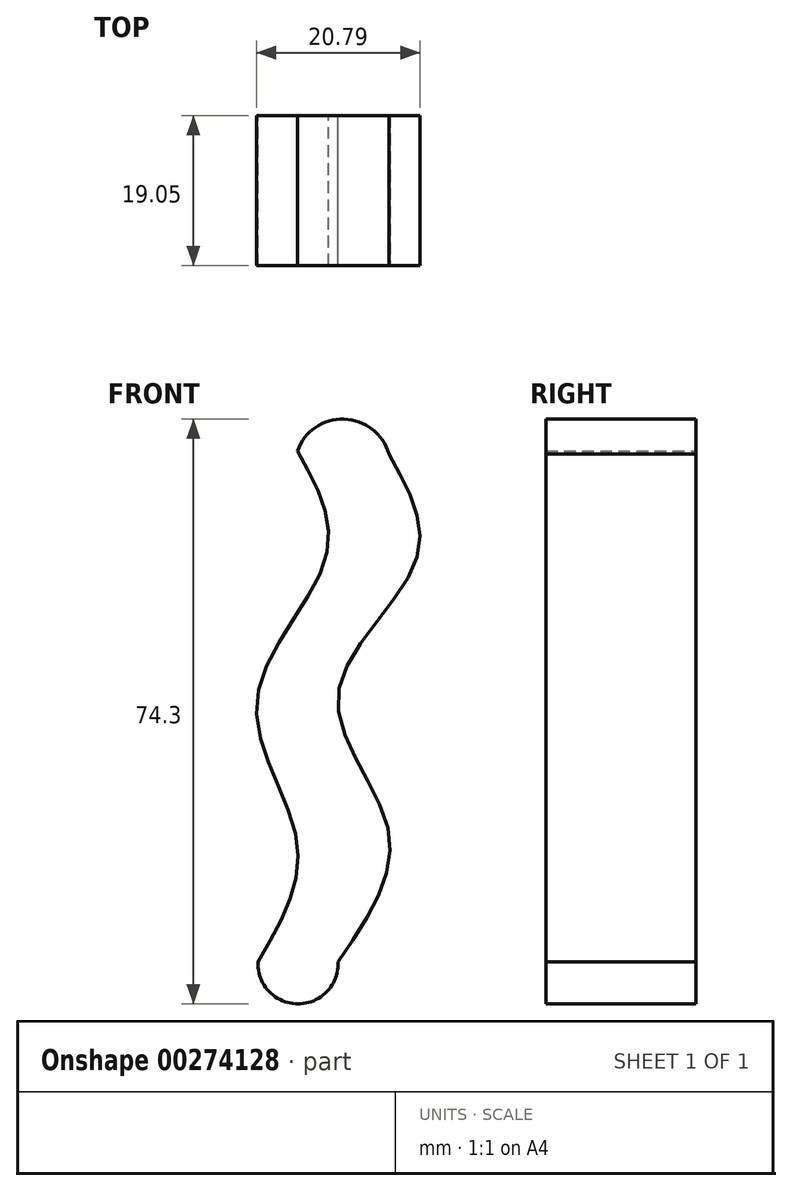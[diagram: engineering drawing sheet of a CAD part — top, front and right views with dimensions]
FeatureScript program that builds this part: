
annotation { "Feature Type Name" : "Feature", "Feature Type Description" : "" }
export const myFeature = defineFeature(function(context is Context, id is Id, definition is map)
    precondition{}
    {
        {
            var Q0;
            Q0=qCreatedBy(makeId("Front.planeOp"),FACE);
            var sketch = newSketch(context, id + "F0", { "sketchPlane" : qUnion([Q0])});
            skArc(sketch, "E0", {"start": v(7.93, 64.52) * mm, "mid": v(2.25, 68.95) * mm, "end": v(-3.69, 64.9) * mm});
            skFitSpline(sketch, "E1", {"points": [v(-3.69, 64.9) * mm, v(0, 51.62) * mm, v(-8.85, 33.18) * mm, v(-3.69, 14.93) * mm, v(-8.66, 0) * mm], "startDerivative": vector(32.5, -57.44) * mm, "endDerivative": vector(-35.53, -60.53) * mm});
            skFitSpline(sketch, "E2", {"points": [v(7.93, 64.52) * mm, v(11.43, 51.07) * mm, v(1.47, 33.92) * mm, v(7.93, 16.4) * mm, v(1.47, 0) * mm], "startDerivative": vector(33.73, -59.55) * mm, "endDerivative": vector(-44.4, -64.45) * mm});
            skArc(sketch, "E3", {"start": v(-8.66, 0) * mm, "mid": v(-3.6, -5.35) * mm, "end": v(1.47, 0) * mm});
            skSolve(sketch);
        }
        {
            var Q0;
            Q0=makeQuery(id+"F0.imprint","IMPRINT",FACE,{"disambiguationData":[TD([[makeQuery(id+"F0.imprint","IMPRINT",EDGE,{"derivedFrom":sQuery(id+"F0.wireOp",EDGE,"E0")}),1.0]])]});
            extrude(context, id + "F1", {"entities" : qUnion([Q0]), "depth" : 19.05 * mm});
        }
    });
